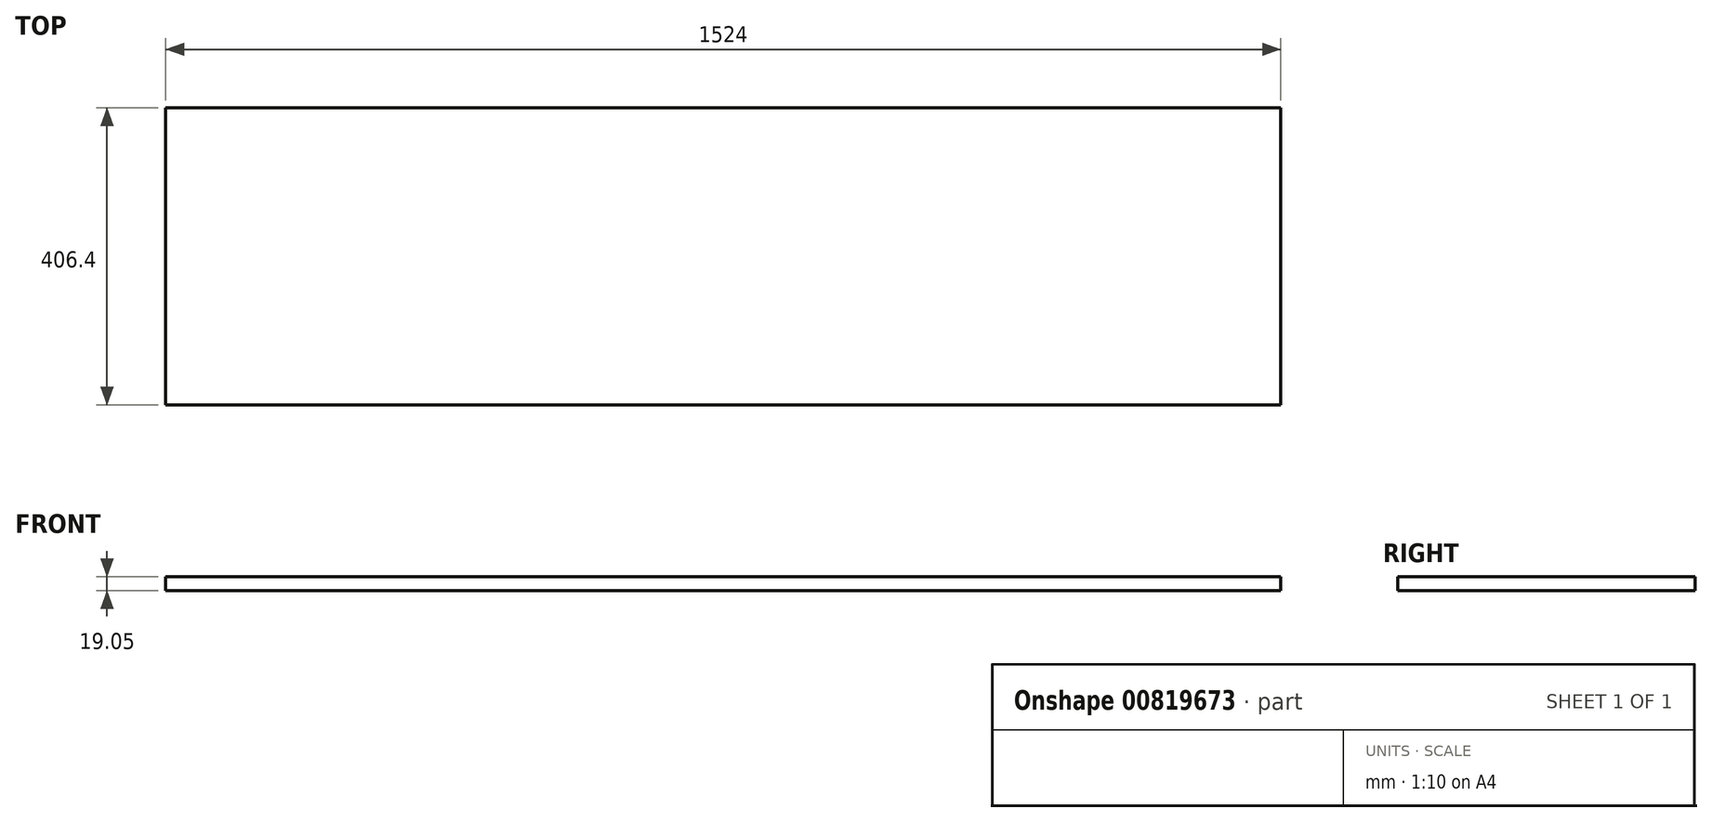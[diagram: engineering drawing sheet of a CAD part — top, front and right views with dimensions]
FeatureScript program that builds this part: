
annotation { "Feature Type Name" : "Feature", "Feature Type Description" : "" }
export const myFeature = defineFeature(function(context is Context, id is Id, definition is map)
    precondition{}
    {
        {
            var Q0;
            Q0=qCreatedBy(makeId("Front.planeOp"),FACE);
            var sketch = newSketch(context, id + "F0", { "sketchPlane" : qUnion([Q0])});
            skLineSegment(sketch, "E0.bottom", {"start": v(0, 0) * mm, "end": v(-1524, 0) * mm});
            skLineSegment(sketch, "E0.top", {"start": v(0, 19.05) * mm, "end": v(-1524, 19.05) * mm});
            skLineSegment(sketch, "E0.left", {"start": v(0, 0) * mm, "end": v(0, 19.05) * mm});
            skLineSegment(sketch, "E0.right", {"start": v(-1524, 0) * mm, "end": v(-1524, 19.05) * mm});
            skSolve(sketch);
        }
        {
            var Q0;
            Q0=makeQuery(id+"F0.imprint","IMPRINT",FACE,{"disambiguationData":[TD([[makeQuery(id+"F0.imprint","IMPRINT",EDGE,{"derivedFrom":sQuery(id+"F0.wireOp",EDGE,"E0.bottom")}),-1.0]])]});
            extrude(context, id + "F1", {"entities" : qUnion([Q0]), "depth" : 406.4 * mm, "offsetDistance" : 25.4 * mm});
        }
    });
